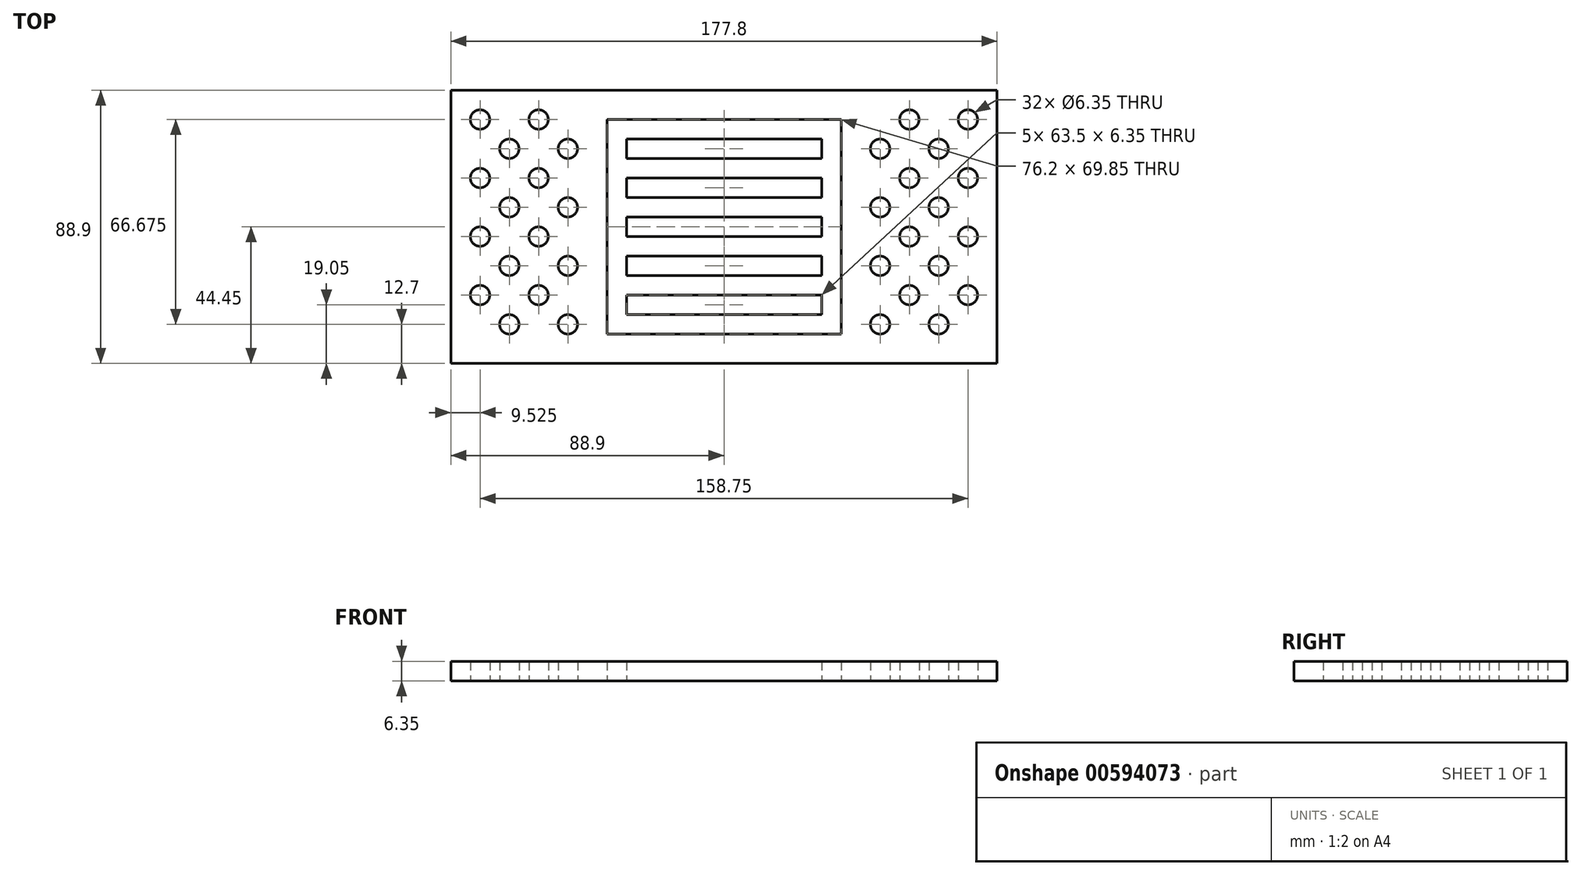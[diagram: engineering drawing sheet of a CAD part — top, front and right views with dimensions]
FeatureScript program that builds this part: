
annotation { "Feature Type Name" : "Feature", "Feature Type Description" : "" }
export const myFeature = defineFeature(function(context is Context, id is Id, definition is map)
    precondition{}
    {
        {
            var Q0;
            Q0=qCreatedBy(makeId("Top.planeOp"),FACE);
            var sketch = newSketch(context, id + "F0", { "sketchPlane" : qUnion([Q0])});
            skLineSegment(sketch, "E0.bottom", {"start": v(0, 0) * mm, "end": v(177.8, 0) * mm});
            skLineSegment(sketch, "E0.top", {"start": v(0, -88.9) * mm, "end": v(177.8, -88.9) * mm});
            skLineSegment(sketch, "E0.left", {"start": v(0, 0) * mm, "end": v(0, -88.9) * mm});
            skLineSegment(sketch, "E0.right", {"start": v(177.8, 0) * mm, "end": v(177.8, -88.9) * mm});
            skLineSegment(sketch, "E1.bottom", {"start": v(50.8, -9.52) * mm, "end": v(127, -9.52) * mm});
            skLineSegment(sketch, "E1.top", {"start": v(50.8, -79.38) * mm, "end": v(127, -79.38) * mm});
            skLineSegment(sketch, "E1.left", {"start": v(50.8, -9.52) * mm, "end": v(50.8, -79.38) * mm});
            skLineSegment(sketch, "E1.right", {"start": v(127, -9.52) * mm, "end": v(127, -79.38) * mm});
            skLineSegment(sketch, "E2.bottom", {"start": v(57.15, -15.88) * mm, "end": v(120.65, -15.88) * mm});
            skLineSegment(sketch, "E2.top", {"start": v(57.15, -22.22) * mm, "end": v(120.65, -22.22) * mm});
            skLineSegment(sketch, "E2.left", {"start": v(57.15, -15.88) * mm, "end": v(57.15, -22.22) * mm});
            skLineSegment(sketch, "E2.right", {"start": v(120.65, -15.88) * mm, "end": v(120.65, -22.22) * mm});
            skLineSegment(sketch, "E3.bottom", {"start": v(57.15, -28.57) * mm, "end": v(120.65, -28.57) * mm});
            skLineSegment(sketch, "E3.top", {"start": v(57.15, -34.92) * mm, "end": v(120.65, -34.92) * mm});
            skLineSegment(sketch, "E3.left", {"start": v(57.15, -28.57) * mm, "end": v(57.15, -34.92) * mm});
            skLineSegment(sketch, "E3.right", {"start": v(120.65, -28.57) * mm, "end": v(120.65, -34.92) * mm});
            skLineSegment(sketch, "E4.bottom", {"start": v(57.15, -41.27) * mm, "end": v(120.65, -41.27) * mm});
            skLineSegment(sketch, "E4.top", {"start": v(57.15, -47.62) * mm, "end": v(120.65, -47.62) * mm});
            skLineSegment(sketch, "E4.left", {"start": v(57.15, -41.27) * mm, "end": v(57.15, -47.62) * mm});
            skLineSegment(sketch, "E4.right", {"start": v(120.65, -41.27) * mm, "end": v(120.65, -47.62) * mm});
            skLineSegment(sketch, "E5.bottom", {"start": v(57.15, -53.98) * mm, "end": v(120.65, -53.98) * mm});
            skLineSegment(sketch, "E5.top", {"start": v(57.15, -60.33) * mm, "end": v(120.65, -60.33) * mm});
            skLineSegment(sketch, "E5.left", {"start": v(57.15, -53.98) * mm, "end": v(57.15, -60.33) * mm});
            skLineSegment(sketch, "E5.right", {"start": v(120.65, -53.98) * mm, "end": v(120.65, -60.33) * mm});
            skLineSegment(sketch, "E6.bottom", {"start": v(57.15, -66.67) * mm, "end": v(120.65, -66.67) * mm});
            skLineSegment(sketch, "E6.top", {"start": v(57.15, -73.02) * mm, "end": v(120.65, -73.02) * mm});
            skLineSegment(sketch, "E6.left", {"start": v(57.15, -66.67) * mm, "end": v(57.15, -73.02) * mm});
            skLineSegment(sketch, "E6.right", {"start": v(120.65, -66.67) * mm, "end": v(120.65, -73.02) * mm});
            skLineSegment(sketch, "E7", {"start": v(88.9, 0) * mm, "end": v(88.9, -6.35) * mm, "construction": true});
            skCircle(sketch, "E8", {"center": v(9.53, -9.53) * mm, "radius": 3.18 * mm});
            skCircle(sketch, "E9", {"center": v(19.05, -19.05) * mm, "radius": 3.18 * mm});
            skCircle(sketch, "E10", {"center": v(28.58, -9.52) * mm, "radius": 3.18 * mm});
            skCircle(sketch, "E11", {"center": v(38.1, -19.05) * mm, "radius": 3.18 * mm});
            skCircle(sketch, "E12", {"center": v(28.58, -28.57) * mm, "radius": 3.18 * mm});
            skCircle(sketch, "E13", {"center": v(9.53, -28.57) * mm, "radius": 3.18 * mm});
            skLineSegment(sketch, "E14", {"start": v(9.53, -28.57) * mm, "end": v(28.58, -28.57) * mm, "construction": true});
            skLineSegment(sketch, "E15", {"start": v(19.05, -19.05) * mm, "end": v(38.1, -19.05) * mm, "construction": true});
            skLineSegment(sketch, "E16", {"start": v(9.53, -9.53) * mm, "end": v(28.58, -9.53) * mm, "construction": true});
            skLineSegment(sketch, "E17", {"start": v(9.52, -9.52) * mm, "end": v(19.05, -19.05) * mm, "construction": true});
            skLineSegment(sketch, "E18", {"start": v(19.05, -19.05) * mm, "end": v(28.58, -28.57) * mm, "construction": true});
            skLineSegment(sketch, "E19", {"start": v(28.58, -9.52) * mm, "end": v(19.05, -19.05) * mm, "construction": true});
            skLineSegment(sketch, "E20", {"start": v(19.05, -19.05) * mm, "end": v(9.53, -28.57) * mm, "construction": true});
            skLineSegment(sketch, "E21", {"start": v(28.58, -9.52) * mm, "end": v(38.1, -19.05) * mm, "construction": true});
            skLineSegment(sketch, "E22", {"start": v(38.1, -19.05) * mm, "end": v(28.58, -28.57) * mm, "construction": true});
            skLineSegment(sketch, "E23", {"start": v(9.53, -9.53) * mm, "end": v(9.53, -28.57) * mm, "construction": true});
            skLineSegment(sketch, "E24", {"start": v(28.58, -9.52) * mm, "end": v(28.58, -28.57) * mm, "construction": true});
            skCircle(sketch, "E25.MirrorC", {"center": v(19.05, -38.1) * mm, "radius": 3.18 * mm});
            skCircle(sketch, "E26.MirrorC", {"center": v(38.1, -38.1) * mm, "radius": 3.18 * mm});
            skCircle(sketch, "E27.MirrorC", {"center": v(9.53, -47.62) * mm, "radius": 3.18 * mm});
            skCircle(sketch, "E28.MirrorC", {"center": v(28.58, -47.62) * mm, "radius": 3.18 * mm});
            skLineSegment(sketch, "E29", {"start": v(9.53, -47.62) * mm, "end": v(28.58, -47.62) * mm, "construction": true});
            skCircle(sketch, "E30.MirrorC", {"center": v(19.05, -57.15) * mm, "radius": 3.18 * mm});
            skCircle(sketch, "E31.MirrorC", {"center": v(38.1, -57.15) * mm, "radius": 3.18 * mm});
            skCircle(sketch, "E32.MirrorC", {"center": v(28.58, -66.67) * mm, "radius": 3.18 * mm});
            skCircle(sketch, "E33.MirrorC", {"center": v(9.53, -66.67) * mm, "radius": 3.18 * mm});
            skCircle(sketch, "E34.MirrorC", {"center": v(19.05, -76.2) * mm, "radius": 3.18 * mm});
            skCircle(sketch, "E35.MirrorC", {"center": v(38.1, -76.2) * mm, "radius": 3.18 * mm});
            skCircle(sketch, "E36.MirrorC", {"center": v(168.28, -9.53) * mm, "radius": 3.18 * mm});
            skCircle(sketch, "E37.MirrorC", {"center": v(149.22, -9.52) * mm, "radius": 3.18 * mm});
            skCircle(sketch, "E38.MirrorC", {"center": v(158.75, -19.05) * mm, "radius": 3.18 * mm});
            skCircle(sketch, "E39.MirrorC", {"center": v(139.7, -19.05) * mm, "radius": 3.18 * mm});
            skCircle(sketch, "E40.MirrorC", {"center": v(149.22, -28.57) * mm, "radius": 3.18 * mm});
            skCircle(sketch, "E41.MirrorC", {"center": v(168.28, -28.57) * mm, "radius": 3.18 * mm});
            skCircle(sketch, "E42.MirrorC", {"center": v(158.75, -38.1) * mm, "radius": 3.18 * mm});
            skCircle(sketch, "E43.MirrorC", {"center": v(158.75, -76.2) * mm, "radius": 3.18 * mm});
            skCircle(sketch, "E44.MirrorC", {"center": v(168.28, -66.67) * mm, "radius": 3.18 * mm});
            skCircle(sketch, "E45.MirrorC", {"center": v(149.22, -66.67) * mm, "radius": 3.18 * mm});
            skCircle(sketch, "E46.MirrorC", {"center": v(158.75, -57.15) * mm, "radius": 3.18 * mm});
            skCircle(sketch, "E47.MirrorC", {"center": v(139.7, -57.15) * mm, "radius": 3.18 * mm});
            skCircle(sketch, "E48.MirrorC", {"center": v(149.22, -47.62) * mm, "radius": 3.18 * mm});
            skCircle(sketch, "E49.MirrorC", {"center": v(168.28, -47.62) * mm, "radius": 3.18 * mm});
            skLineSegment(sketch, "E50", {"start": v(149.22, -28.57) * mm, "end": v(149.22, -47.62) * mm, "construction": true});
            skCircle(sketch, "E51.MirrorC", {"center": v(139.7, -38.1) * mm, "radius": 3.18 * mm});
            skCircle(sketch, "E52.MirrorC", {"center": v(139.7, -76.2) * mm, "radius": 3.18 * mm});
            skSolve(sketch);
        }
        {
            var Q0;
            Q0=makeQuery(id+"F0.imprint","IMPRINT",FACE,{"disambiguationData":[TD([[makeQuery(id+"F0.imprint","IMPRINT",EDGE,{"derivedFrom":sQuery(id+"F0.wireOp",EDGE,"E0.bottom")}),-1.0]])]});
            extrude(context, id + "F1", {"entities" : qUnion([Q0]), "depth" : 6.35 * mm, "offsetDistance" : 25.4 * mm});
        }
        {
            var Q0;
            Q0=makeQuery(id+"F0.imprint","IMPRINT",FACE,{"disambiguationData":[TD([[makeQuery(id+"F0.imprint","IMPRINT",EDGE,{"derivedFrom":sQuery(id+"F0.wireOp",EDGE,"E1.bottom")}),-1.0]])]});
            extrude(context, id + "F2", {"entities" : qUnion([Q0]), "depth" : 6.35 * mm, "offsetDistance" : 25.4 * mm});
        }
    });
